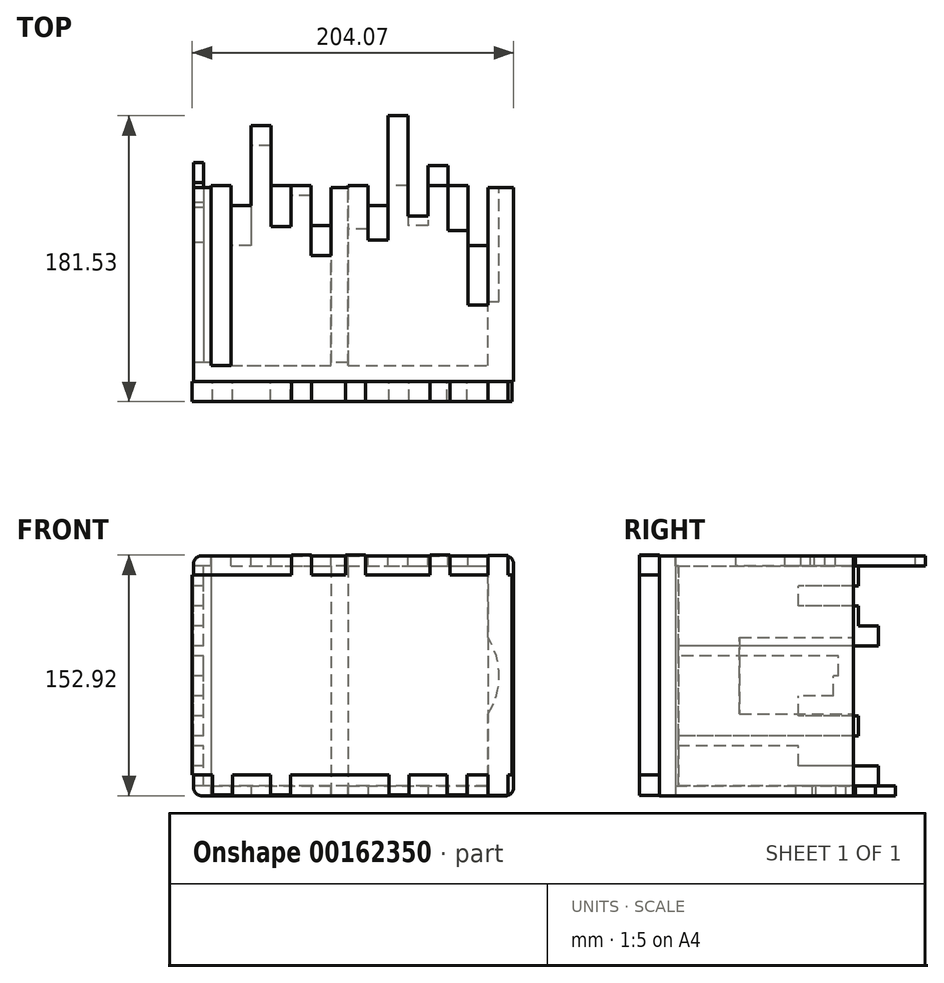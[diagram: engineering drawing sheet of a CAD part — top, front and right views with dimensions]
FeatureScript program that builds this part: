
annotation { "Feature Type Name" : "Feature", "Feature Type Description" : "" }
export const myFeature = defineFeature(function(context is Context, id is Id, definition is map)
    precondition{}
    {
        {
            var Q0;
            Q0=qCreatedBy(makeId("Front.planeOp"),FACE);
            var sketch = newSketch(context, id + "F0", { "sketchPlane" : qUnion([Q0])});
            skLineSegment(sketch, "E0.bottom", {"start": v(101.6, -76.2) * mm, "end": v(-101.6, -76.2) * mm});
            skLineSegment(sketch, "E0.top", {"start": v(101.6, 76.2) * mm, "end": v(-101.6, 76.2) * mm});
            skLineSegment(sketch, "E0.left", {"start": v(101.6, -76.2) * mm, "end": v(101.6, 76.2) * mm});
            skLineSegment(sketch, "E0.right", {"start": v(-101.6, -76.2) * mm, "end": v(-101.6, 76.2) * mm});
            skPoint(sketch, "E0.middle", {"position": v(0, 0) * mm});
            skSolve(sketch);
        }
        {
            var Q0;
            Q0=makeQuery(id+"F0.imprint","IMPRINT",FACE,{"disambiguationData":[TD([[makeQuery(id+"F0.imprint","IMPRINT",EDGE,{"derivedFrom":sQuery(id+"F0.wireOp",EDGE,"E0.bottom")}),-1.0]])]});
            var sketch = newSketch(context, id + "F1", { "sketchPlane" : qUnion([Q0])});
            skLineSegment(sketch, "E1.bottom", {"start": v(95.25, 69.94) * mm, "end": v(0, 69.94) * mm});
            skLineSegment(sketch, "E1.top", {"start": v(95.25, -69.76) * mm, "end": v(0, -69.76) * mm});
            skLineSegment(sketch, "E1.left", {"start": v(95.25, 69.94) * mm, "end": v(95.25, -69.76) * mm});
            skLineSegment(sketch, "E1.right", {"start": v(0, 69.94) * mm, "end": v(0, -69.76) * mm});
            skCircle(sketch, "E2", {"center": v(48.06, 0) * mm, "radius": 44.45 * mm});
            skSolve(sketch);
        }
        {
            var Q0;
            Q0=makeQuery(id+"F0.imprint","IMPRINT",FACE,{"disambiguationData":[TD([[makeQuery(id+"F0.imprint","IMPRINT",EDGE,{"derivedFrom":sQuery(id+"F0.wireOp",EDGE,"E0.bottom")}),-1.0]])]});
            extrude(context, id + "F2", {"entities" : qUnion([Q0]), "depth" : 152.4 * mm});
        }
        {
            var Q0;
            Q0=qCreatedBy(makeId("Front.planeOp"),FACE);
            var sketch = newSketch(context, id + "F3", { "sketchPlane" : qUnion([Q0])});
            skLineSegment(sketch, "E3.bottom", {"start": v(-6.15, 69.63) * mm, "end": v(-95.05, 69.63) * mm});
            skLineSegment(sketch, "E3.top", {"start": v(-6.15, -70.07) * mm, "end": v(-95.05, -70.07) * mm});
            skLineSegment(sketch, "E3.left", {"start": v(-6.15, 69.63) * mm, "end": v(-6.15, -70.07) * mm});
            skLineSegment(sketch, "E3.right", {"start": v(-95.05, 69.63) * mm, "end": v(-95.05, -70.07) * mm});
            skSolve(sketch);
        }
        {
            var Q0;
            Q0 = qSketchRegion(id + "F3", true);
            extrude(context, id + "F4", {"entities" : qUnion([Q0]), "operationType" : NewBodyOperationType.REMOVE, "depth" : 12.7 * mm});
        }
        {
            var Q0;
            Q0=makeQuery(id+"F4.boolean.opBoolean","COPY",FACE,{"derivedFrom":makeQuery(id+"F4.opExtrude","CAP_FACE",FACE,{"disambiguationData":[OSD([sQuery(id+"F3.wireOp",EDGE,"E3.bottom"),sQuery(id+"F3.wireOp",EDGE,"E3.top"),sQuery(id+"F3.wireOp",EDGE,"E3.left"),sQuery(id+"F3.wireOp",EDGE,"E3.right")])],"isStart":false})});
            var sketch = newSketch(context, id + "F5", { "sketchPlane" : qUnion([Q0])});
            skCircle(sketch, "E4", {"center": v(19.23, 52.88) * mm, "radius": 6.35 * mm});
            skCircle(sketch, "E5.0.1.0", {"center": v(19.23, 31.3) * mm, "radius": 6.35 * mm});
            skCircle(sketch, "E5.0.2.0", {"center": v(19.23, 9.7) * mm, "radius": 6.35 * mm});
            skCircle(sketch, "E5.0.3.0", {"center": v(19.23, -11.89) * mm, "radius": 6.35 * mm});
            skCircle(sketch, "E5.0.4.0", {"center": v(19.23, -33.48) * mm, "radius": 6.35 * mm});
            skCircle(sketch, "E5.0.5.0", {"center": v(19.23, -55.07) * mm, "radius": 6.35 * mm});
            skCircle(sketch, "E5.1.0.0", {"center": v(40.82, 52.88) * mm, "radius": 6.35 * mm});
            skCircle(sketch, "E5.1.1.0", {"center": v(40.82, 31.3) * mm, "radius": 6.35 * mm});
            skCircle(sketch, "E5.1.2.0", {"center": v(40.82, 9.7) * mm, "radius": 6.35 * mm});
            skCircle(sketch, "E5.1.3.0", {"center": v(40.82, -11.89) * mm, "radius": 6.35 * mm});
            skCircle(sketch, "E5.1.4.0", {"center": v(40.82, -33.48) * mm, "radius": 6.35 * mm});
            skCircle(sketch, "E5.1.5.0", {"center": v(40.82, -55.07) * mm, "radius": 6.35 * mm});
            skCircle(sketch, "E5.2.0.0", {"center": v(62.41, 52.88) * mm, "radius": 6.35 * mm});
            skCircle(sketch, "E5.2.1.0", {"center": v(62.41, 31.3) * mm, "radius": 6.35 * mm});
            skCircle(sketch, "E5.2.2.0", {"center": v(62.41, 9.7) * mm, "radius": 6.35 * mm});
            skCircle(sketch, "E5.2.3.0", {"center": v(62.41, -11.89) * mm, "radius": 6.35 * mm});
            skCircle(sketch, "E5.2.4.0", {"center": v(62.41, -33.48) * mm, "radius": 6.35 * mm});
            skCircle(sketch, "E5.2.5.0", {"center": v(62.41, -55.07) * mm, "radius": 6.35 * mm});
            skCircle(sketch, "E5.3.0.0", {"center": v(84, 52.88) * mm, "radius": 6.35 * mm});
            skCircle(sketch, "E5.3.1.0", {"center": v(84, 31.3) * mm, "radius": 6.35 * mm});
            skCircle(sketch, "E5.3.2.0", {"center": v(84, 9.7) * mm, "radius": 6.35 * mm});
            skCircle(sketch, "E5.3.3.0", {"center": v(84, -11.89) * mm, "radius": 6.35 * mm});
            skCircle(sketch, "E5.3.4.0", {"center": v(84, -33.48) * mm, "radius": 6.35 * mm});
            skCircle(sketch, "E5.3.5.0", {"center": v(84, -55.07) * mm, "radius": 6.35 * mm});
            skLineSegment(sketch, "E5.direction1", {"start": v(19.23, 52.88) * mm, "end": v(40.82, 52.88) * mm, "construction": true});
            skLineSegment(sketch, "E5.direction2", {"start": v(19.23, 52.88) * mm, "end": v(19.23, 31.3) * mm, "construction": true});
            skSolve(sketch);
        }
        {
            var Q0;
            Q0 = qSketchRegion(id + "F5", true);
            extrude(context, id + "F6", {"entities" : qUnion([Q0]), "operationType" : NewBodyOperationType.REMOVE, "oppositeDirection" : true, "depth" : 127 * mm});
        }
        {
            var Q0;
            Q0=makeQuery(id+"F2.opExtrude","CAP_FACE",FACE,{"disambiguationData":[OSD([sQuery(id+"F0.wireOp",EDGE,"E0.bottom"),sQuery(id+"F0.wireOp",EDGE,"E0.top"),sQuery(id+"F0.wireOp",EDGE,"E0.left"),sQuery(id+"F0.wireOp",EDGE,"E0.right")])],"isStart":false});
            var sketch = newSketch(context, id + "F7", { "sketchPlane" : qUnion([Q0])});
            skLineSegment(sketch, "E6.bottom", {"start": v(76.89, -54.4) * mm, "end": v(-76.89, -54.4) * mm});
            skLineSegment(sketch, "E6.top", {"start": v(76.89, 54.4) * mm, "end": v(-76.89, 54.4) * mm});
            skLineSegment(sketch, "E6.left", {"start": v(76.89, -54.4) * mm, "end": v(76.89, 54.4) * mm});
            skLineSegment(sketch, "E6.right", {"start": v(-76.89, -54.4) * mm, "end": v(-76.89, 54.4) * mm});
            skPoint(sketch, "E6.middle", {"position": v(0, 0) * mm});
            skSolve(sketch);
        }
        {
            var Q0;
            Q0=makeQuery(id+"F1.imprint","IMPRINT",FACE,{"disambiguationData":[TD([[makeQuery(id+"F1.imprint","IMPRINT",EDGE,{"derivedFrom":sQuery(id+"F1.wireOp",EDGE,"E2")}),1.0]])]});
            extrude(context, id + "F8", {"entities" : qUnion([Q0]), "operationType" : NewBodyOperationType.REMOVE, "depth" : 101.6 * mm});
        }
        {
            var Q0;
            Q0=makeQuery(id+"F2.opExtrude","CAP_EDGE",EDGE,{"disambiguationData":[OSD([sQuery(id+"F0.wireOp",EDGE,"E0.top")])],"isStart":true});
            var Q1;
            Q1=makeQuery(id+"F2.opExtrude","CAP_EDGE",EDGE,{"disambiguationData":[OSD([sQuery(id+"F0.wireOp",EDGE,"E0.left")])],"isStart":true});
            var Q2;
            Q2=makeQuery(id+"F2.opExtrude","CAP_EDGE",EDGE,{"disambiguationData":[OSD([sQuery(id+"F0.wireOp",EDGE,"E0.bottom")])],"isStart":true});
            var Q3;
            Q3=makeQuery(id+"F2.opExtrude","CAP_EDGE",EDGE,{"disambiguationData":[OSD([sQuery(id+"F0.wireOp",EDGE,"E0.right")])],"isStart":true});
            var Q4;
            Q4=makeQuery(id+"F2.opExtrude","SWEPT_EDGE",EDGE,{"disambiguationData":[OSD([sQuery(id+"F0.wireOp",EDGE,"E0.bottom"),sQuery(id+"F0.wireOp",EDGE,"E0.right")])]});
            var Q5;
            Q5=makeQuery(id+"F2.opExtrude","SWEPT_EDGE",EDGE,{"disambiguationData":[OSD([sQuery(id+"F0.wireOp",EDGE,"E0.bottom"),sQuery(id+"F0.wireOp",EDGE,"E0.left")])]});
            var Q6;
            Q6=makeQuery(id+"F2.opExtrude","SWEPT_EDGE",EDGE,{"disambiguationData":[OSD([sQuery(id+"F0.wireOp",EDGE,"E0.top"),sQuery(id+"F0.wireOp",EDGE,"E0.left")])]});
            var Q7;
            Q7=makeQuery(id+"F2.opExtrude","SWEPT_EDGE",EDGE,{"disambiguationData":[OSD([sQuery(id+"F0.wireOp",EDGE,"E0.top"),sQuery(id+"F0.wireOp",EDGE,"E0.right")])]});
            fillet(context, id + "F9", {"entities" : qUnion([Q0, Q1, Q2, Q3, Q4, Q5, Q6, Q7]), "radius" : 5.08 * mm, "tangentPropagation" : true, "allowEdgeOverflow" : false});
        }
        {
            var Q0;
            Q0=makeQuery(id+"F2.opExtrude","SWEPT_FACE",FACE,{"disambiguationData":[OSD([sQuery(id+"F0.wireOp",EDGE,"E0.right")])]});
            var sketch = newSketch(context, id + "F10", { "sketchPlane" : qUnion([Q0])});
            skLineSegment(sketch, "E7.bottom", {"start": v(140.43, -69.85) * mm, "end": v(13.43, -69.85) * mm});
            skLineSegment(sketch, "E7.top", {"start": v(140.43, 69.85) * mm, "end": v(13.43, 69.85) * mm});
            skLineSegment(sketch, "E7.left", {"start": v(140.43, -69.85) * mm, "end": v(140.43, 69.85) * mm});
            skLineSegment(sketch, "E7.right", {"start": v(13.43, -69.85) * mm, "end": v(13.43, 69.85) * mm});
            skPoint(sketch, "E7.middle", {"position": v(76.93, 0) * mm});
            skLineSegment(sketch, "E8.0.0", {"start": v(12.7, 69.63) * mm, "end": v(12.7, -70.07) * mm});
            skLineSegment(sketch, "E8.0.2", {"start": v(12.7, -70.07) * mm, "end": v(12.7, 69.63) * mm});
            skLineSegment(sketch, "E8.1.0", {"start": v(0, 71.12) * mm, "end": v(0, -71.12) * mm});
            skLineSegment(sketch, "E8.1.2", {"start": v(0, -71.12) * mm, "end": v(0, 71.12) * mm});
            skArc(sketch, "E8.2.0", {"start": v(0, 71.12) * mm, "mid": v(1.49, 74.71) * mm, "end": v(5.08, 76.2) * mm});
            skArc(sketch, "E8.2.2", {"start": v(5.08, 76.2) * mm, "mid": v(1.49, 74.71) * mm, "end": v(0, 71.12) * mm});
            skLineSegment(sketch, "E8.3.0", {"start": v(0, 71.12) * mm, "end": v(5.08, 71.12) * mm});
            skLineSegment(sketch, "E8.3.1", {"start": v(5.08, 71.12) * mm, "end": v(5.08, -71.12) * mm});
            skLineSegment(sketch, "E8.3.2", {"start": v(5.08, -71.12) * mm, "end": v(0, -71.12) * mm});
            skLineSegment(sketch, "E8.3.3", {"start": v(0, 71.12) * mm, "end": v(0, -71.12) * mm});
            skArc(sketch, "E8.4.0", {"start": v(5.08, -76.2) * mm, "mid": v(1.49, -74.71) * mm, "end": v(0, -71.12) * mm});
            skArc(sketch, "E8.4.2", {"start": v(0, -71.12) * mm, "mid": v(1.49, -74.71) * mm, "end": v(5.08, -76.2) * mm});
            skLineSegment(sketch, "E8.5.0", {"start": v(5.08, 71.12) * mm, "end": v(0, 71.12) * mm});
            skLineSegment(sketch, "E8.5.1", {"start": v(0, 71.12) * mm, "end": v(0, -71.12) * mm});
            skLineSegment(sketch, "E8.5.2", {"start": v(0, -71.12) * mm, "end": v(5.08, -71.12) * mm});
            skLineSegment(sketch, "E8.5.3", {"start": v(5.08, 71.12) * mm, "end": v(5.08, -71.12) * mm});
            skSolve(sketch);
        }
        {
            var Q0;
            Q0=makeQuery(id+"F10.imprint","IMPRINT",FACE,{"disambiguationData":[TD([[makeQuery(id+"F10.imprint","IMPRINT",EDGE,{"derivedFrom":sQuery(id+"F10.wireOp",EDGE,"E7.bottom")}),-1.0]])]});
            extrude(context, id + "F11", {"entities" : qUnion([Q0]), "operationType" : NewBodyOperationType.REMOVE, "oppositeDirection" : true, "depth" : 101.6 * mm});
        }
        {
            var Q0;
            Q0=makeQuery(id+"F2.opExtrude","CAP_FACE",FACE,{"disambiguationData":[OSD([sQuery(id+"F0.wireOp",EDGE,"E0.bottom"),sQuery(id+"F0.wireOp",EDGE,"E0.top"),sQuery(id+"F0.wireOp",EDGE,"E0.left"),sQuery(id+"F0.wireOp",EDGE,"E0.right")])],"isStart":true});
            var sketch = newSketch(context, id + "F12", { "sketchPlane" : qUnion([Q0])});
            skCircle(sketch, "E9", {"center": v(-87.4, 62.09) * mm, "radius": 6.35 * mm});
            skSolve(sketch);
        }
        {
            var Q0;
            Q0=makeQuery(id+"F2.opExtrude","SWEPT_FACE",FACE,{"disambiguationData":[OSD([sQuery(id+"F0.wireOp",EDGE,"E0.bottom")])]});
            var sketch = newSketch(context, id + "F13", { "sketchPlane" : qUnion([Q0])});
            skLineSegment(sketch, "E10.bottom", {"start": v(-90.54, 142.26) * mm, "end": v(-14.34, 142.26) * mm});
            skLineSegment(sketch, "E10.top", {"start": v(-90.54, 15.26) * mm, "end": v(-14.34, 15.26) * mm});
            skLineSegment(sketch, "E10.left", {"start": v(-90.54, 142.26) * mm, "end": v(-90.54, 15.26) * mm});
            skLineSegment(sketch, "E10.right", {"start": v(-14.34, 142.26) * mm, "end": v(-14.34, 15.26) * mm});
            skPoint(sketch, "E10.middle", {"position": v(-52.44, 78.76) * mm});
            skSolve(sketch);
        }
        {
            var Q0;
            Q0=makeQuery(id+"F12.imprint","IMPRINT",FACE,{"disambiguationData":[TD([[makeQuery(id+"F12.imprint","IMPRINT",EDGE,{"derivedFrom":sQuery(id+"F12.wireOp",EDGE,"E9")}),-1.0]])]});
            var sketch = newSketch(context, id + "F14", { "sketchPlane" : qUnion([Q0])});
            skLineSegment(sketch, "E11.bottom", {"start": v(-156.27, 104.96) * mm, "end": v(156.27, 104.96) * mm});
            skLineSegment(sketch, "E11.top", {"start": v(-156.27, -104.96) * mm, "end": v(156.27, -104.96) * mm});
            skLineSegment(sketch, "E11.left", {"start": v(-156.27, 104.96) * mm, "end": v(-156.27, -104.96) * mm});
            skLineSegment(sketch, "E11.right", {"start": v(156.27, 104.96) * mm, "end": v(156.27, -104.96) * mm});
            skPoint(sketch, "E11.middle", {"position": v(0, 0) * mm});
            skPoint(sketch, "E12.middle", {"position": v(298.59, 26.28) * mm});
            skSolve(sketch);
        }
        {
            var Q0;
            Q0=makeQuery(id+"F12.imprint","IMPRINT",FACE,{"disambiguationData":[TD([[makeQuery(id+"F12.imprint","IMPRINT",EDGE,{"derivedFrom":sQuery(id+"F12.wireOp",EDGE,"E9")}),-1.0]])]});
            var Q1;
            Q1=makeQuery(id+"F14.imprint","IMPRINT",FACE,{"disambiguationData":[TD([[makeQuery(id+"F14.imprint","IMPRINT",EDGE,{"derivedFrom":makeQuery(id+"F12.imprint","IMPRINT",EDGE,{"derivedFrom":makeQuery(id+"F4.boolean.opBoolean","COPY",EDGE,{"derivedFrom":makeQuery(id+"F4.opExtrude","CAP_EDGE",EDGE,{"disambiguationData":[OSD([sQuery(id+"F3.wireOp",EDGE,"E3.bottom")])],"isStart":true})})})}),-1.0]])]});
            var Q2;
            Q2 = qSketchRegion(id + "F14", true);
            extrude(context, id + "F15", {"entities" : qUnion([Q0, Q1, Q2]), "operationType" : NewBodyOperationType.REMOVE, "oppositeDirection" : true, "depth" : 29.2 * mm});
        }
        {
            var Q0;
            Q0 = qSketchRegion(id + "F13", true);
            extrude(context, id + "F16", {"entities" : qUnion([Q0]), "operationType" : NewBodyOperationType.REMOVE, "oppositeDirection" : true, "depth" : 152.4 * mm});
        }
        {
            var Q0;
            Q0=qCreatedBy(makeId("Top.planeOp"),FACE);
            var sketch = newSketch(context, id + "F17", { "sketchPlane" : qUnion([Q0])});
            skLineSegment(sketch, "E13.bottom", {"start": v(-3.6, -142.32) * mm, "end": v(85.3, -142.32) * mm});
            skLineSegment(sketch, "E13.top", {"start": v(-3.6, -15.32) * mm, "end": v(85.3, -15.32) * mm});
            skLineSegment(sketch, "E13.left", {"start": v(-3.6, -142.32) * mm, "end": v(-3.6, -15.32) * mm});
            skLineSegment(sketch, "E13.right", {"start": v(85.3, -142.32) * mm, "end": v(85.3, -15.32) * mm});
            skPoint(sketch, "E13.middle", {"position": v(40.84, -78.82) * mm});
            skSolve(sketch);
        }
        {
            var Q0;
            Q0 = qSketchRegion(id + "F17", true);
            extrude(context, id + "F18", {"entities" : qUnion([Q0]), "operationType" : NewBodyOperationType.REMOVE, "endBound" : BoundingType.SYMMETRIC, "depth" : 507.24 * mm});
        }
        {
            var Q0;
            Q0=makeQuery(id+"F2.opExtrude","SWEPT_FACE",FACE,{"disambiguationData":[OSD([sQuery(id+"F0.wireOp",EDGE,"E0.top")])]});
            var sketch = newSketch(context, id + "F19", { "sketchPlane" : qUnion([Q0])});
            skLineSegment(sketch, "E14.bottom", {"start": v(-90.54, -142.26) * mm, "end": v(-77.84, -142.26) * mm});
            skLineSegment(sketch, "E14.top", {"start": v(-90.54, -91.46) * mm, "end": v(-77.84, -91.46) * mm});
            skLineSegment(sketch, "E14.left", {"start": v(-90.54, -142.26) * mm, "end": v(-90.54, -91.46) * mm});
            skLineSegment(sketch, "E14.right", {"start": v(-77.84, -142.26) * mm, "end": v(-77.84, -91.46) * mm});
            skPoint(sketch, "E14.middle", {"position": v(-84.2, -116.86) * mm});
            skLineSegment(sketch, "E15.bottom", {"start": v(-77.84, -40.66) * mm, "end": v(-65.14, -40.66) * mm});
            skLineSegment(sketch, "E15.top", {"start": v(-77.84, -142.26) * mm, "end": v(-65.14, -142.26) * mm});
            skLineSegment(sketch, "E15.left", {"start": v(-77.84, -40.66) * mm, "end": v(-77.84, -142.26) * mm});
            skLineSegment(sketch, "E15.right", {"start": v(-65.14, -40.66) * mm, "end": v(-65.14, -142.26) * mm});
            skLineSegment(sketch, "E16.bottom", {"start": v(-65.14, 10.14) * mm, "end": v(-52.44, 10.14) * mm});
            skLineSegment(sketch, "E16.top", {"start": v(-65.14, -142.26) * mm, "end": v(-52.44, -142.26) * mm});
            skLineSegment(sketch, "E16.left", {"start": v(-65.14, 10.14) * mm, "end": v(-65.14, -142.26) * mm});
            skLineSegment(sketch, "E16.right", {"start": v(-52.44, 10.14) * mm, "end": v(-52.44, -142.26) * mm});
            skLineSegment(sketch, "E17.bottom", {"start": v(-52.44, -53.83) * mm, "end": v(-39.74, -53.83) * mm});
            skLineSegment(sketch, "E17.top", {"start": v(-52.44, -142.26) * mm, "end": v(-39.74, -142.26) * mm});
            skLineSegment(sketch, "E17.left", {"start": v(-52.44, -53.83) * mm, "end": v(-52.44, -142.26) * mm});
            skLineSegment(sketch, "E17.right", {"start": v(-39.74, -53.83) * mm, "end": v(-39.74, -142.26) * mm});
            skLineSegment(sketch, "E18.bottom", {"start": v(-39.74, -27.96) * mm, "end": v(-27.04, -27.96) * mm});
            skLineSegment(sketch, "E18.top", {"start": v(-39.74, -142.26) * mm, "end": v(-27.04, -142.26) * mm});
            skLineSegment(sketch, "E18.left", {"start": v(-39.74, -27.96) * mm, "end": v(-39.74, -142.26) * mm});
            skLineSegment(sketch, "E18.right", {"start": v(-27.04, -27.96) * mm, "end": v(-27.04, -142.26) * mm});
            skLineSegment(sketch, "E19.bottom", {"start": v(-27.04, -72.53) * mm, "end": v(-14.34, -72.53) * mm});
            skLineSegment(sketch, "E19.top", {"start": v(-27.04, -142.26) * mm, "end": v(-14.34, -142.26) * mm});
            skLineSegment(sketch, "E19.left", {"start": v(-27.04, -72.53) * mm, "end": v(-27.04, -142.26) * mm});
            skLineSegment(sketch, "E19.right", {"start": v(-14.34, -72.53) * mm, "end": v(-14.34, -142.26) * mm});
            skLineSegment(sketch, "E20.bottom", {"start": v(-3.6, -28.02) * mm, "end": v(9.1, -28.02) * mm});
            skLineSegment(sketch, "E20.top", {"start": v(-3.6, -142.32) * mm, "end": v(9.1, -142.32) * mm});
            skLineSegment(sketch, "E20.left", {"start": v(-3.6, -28.02) * mm, "end": v(-3.6, -142.32) * mm});
            skLineSegment(sketch, "E20.right", {"start": v(9.1, -28.02) * mm, "end": v(9.1, -142.32) * mm});
            skLineSegment(sketch, "E21.bottom", {"start": v(9.1, -62.44) * mm, "end": v(21.8, -62.44) * mm});
            skLineSegment(sketch, "E21.top", {"start": v(9.1, -142.32) * mm, "end": v(21.8, -142.32) * mm});
            skLineSegment(sketch, "E21.left", {"start": v(9.1, -62.44) * mm, "end": v(9.1, -142.32) * mm});
            skLineSegment(sketch, "E21.right", {"start": v(21.8, -62.44) * mm, "end": v(21.8, -142.32) * mm});
            skLineSegment(sketch, "E22.bottom", {"start": v(21.8, 16.43) * mm, "end": v(34.5, 16.43) * mm});
            skLineSegment(sketch, "E22.top", {"start": v(21.8, -142.32) * mm, "end": v(34.5, -142.32) * mm});
            skLineSegment(sketch, "E22.left", {"start": v(21.8, 16.43) * mm, "end": v(21.8, -142.32) * mm});
            skLineSegment(sketch, "E22.right", {"start": v(34.5, 16.43) * mm, "end": v(34.5, -142.32) * mm});
            skLineSegment(sketch, "E23.bottom", {"start": v(34.5, -47.24) * mm, "end": v(47.2, -47.24) * mm});
            skLineSegment(sketch, "E23.top", {"start": v(34.5, -142.32) * mm, "end": v(47.2, -142.32) * mm});
            skLineSegment(sketch, "E23.left", {"start": v(34.5, -47.24) * mm, "end": v(34.5, -142.32) * mm});
            skLineSegment(sketch, "E23.right", {"start": v(47.2, -47.24) * mm, "end": v(47.2, -142.32) * mm});
            skLineSegment(sketch, "E24.bottom", {"start": v(47.2, -28.02) * mm, "end": v(59.9, -28.02) * mm});
            skLineSegment(sketch, "E24.top", {"start": v(47.2, -142.32) * mm, "end": v(59.9, -142.32) * mm});
            skLineSegment(sketch, "E24.left", {"start": v(47.2, -28.02) * mm, "end": v(47.2, -142.32) * mm});
            skLineSegment(sketch, "E24.right", {"start": v(59.9, -28.02) * mm, "end": v(59.9, -142.32) * mm});
            skLineSegment(sketch, "E25.bottom", {"start": v(59.9, -56.63) * mm, "end": v(72.6, -56.63) * mm});
            skLineSegment(sketch, "E25.top", {"start": v(59.9, -142.32) * mm, "end": v(72.6, -142.32) * mm});
            skLineSegment(sketch, "E25.left", {"start": v(59.9, -56.63) * mm, "end": v(59.9, -142.32) * mm});
            skLineSegment(sketch, "E25.right", {"start": v(72.6, -56.63) * mm, "end": v(72.6, -142.32) * mm});
            skLineSegment(sketch, "E26.bottom", {"start": v(72.6, -103.72) * mm, "end": v(85.3, -103.72) * mm});
            skLineSegment(sketch, "E26.top", {"start": v(72.6, -142.32) * mm, "end": v(85.3, -142.32) * mm});
            skLineSegment(sketch, "E26.left", {"start": v(72.6, -103.72) * mm, "end": v(72.6, -142.32) * mm});
            skLineSegment(sketch, "E26.right", {"start": v(85.3, -103.72) * mm, "end": v(85.3, -142.32) * mm});
            skSolve(sketch);
        }
        {
            var Q0;
            Q0=makeQuery(id+"F19.imprint","IMPRINT",FACE,{"disambiguationData":[TD([[makeQuery(id+"F19.imprint","IMPRINT",EDGE,{"derivedFrom":sQuery(id+"F19.wireOp",EDGE,"E26.bottom")}),-1.0]])]});
            var Q1;
            {var subQ3=sQuery(id+"F19.wireOp",EDGE,"E24.bottom");Q1=makeQuery(id+"F19.imprint","IMPRINT",FACE,{"disambiguationData":[TD([[makeQuery(id+"F19.imprint","IMPRINT",EDGE,{"derivedFrom":subQ3}),-1.0]])]});}
            var Q2;
            Q2=makeQuery(id+"F19.imprint","IMPRINT",FACE,{"disambiguationData":[TD([[makeQuery(id+"F19.imprint","IMPRINT",EDGE,{"derivedFrom":sQuery(id+"F19.wireOp",EDGE,"E25.bottom")}),-1.0]])]});
            var Q3;
            {var subQ0=sQuery(id+"F19.wireOp",EDGE,"E23.bottom");Q3=makeQuery(id+"F19.imprint","IMPRINT",FACE,{"disambiguationData":[TD([[makeQuery(id+"F19.imprint","IMPRINT",EDGE,{"derivedFrom":subQ0}),-1.0]])]});}
            var Q4;
            {var subQ3=sQuery(id+"F19.wireOp",EDGE,"E22.bottom");Q4=makeQuery(id+"F19.imprint","IMPRINT",FACE,{"disambiguationData":[TD([[makeQuery(id+"F19.imprint","IMPRINT",EDGE,{"derivedFrom":subQ3}),-1.0]])]});}
            var Q5;
            {var subQ0=sQuery(id+"F19.wireOp",EDGE,"E21.bottom");Q5=makeQuery(id+"F19.imprint","IMPRINT",FACE,{"disambiguationData":[TD([[makeQuery(id+"F19.imprint","IMPRINT",EDGE,{"derivedFrom":subQ0}),-1.0]])]});}
            var Q6;
            Q6=makeQuery(id+"F19.imprint","IMPRINT",FACE,{"disambiguationData":[TD([[makeQuery(id+"F19.imprint","IMPRINT",EDGE,{"derivedFrom":sQuery(id+"F19.wireOp",EDGE,"E19.bottom")}),-1.0]])]});
            var Q7;
            {var subQ3=sQuery(id+"F19.wireOp",EDGE,"E18.bottom");Q7=makeQuery(id+"F19.imprint","IMPRINT",FACE,{"disambiguationData":[TD([[makeQuery(id+"F19.imprint","IMPRINT",EDGE,{"derivedFrom":subQ3}),-1.0]])]});}
            var Q8;
            {var subQ0=sQuery(id+"F19.wireOp",EDGE,"E17.bottom");Q8=makeQuery(id+"F19.imprint","IMPRINT",FACE,{"disambiguationData":[TD([[makeQuery(id+"F19.imprint","IMPRINT",EDGE,{"derivedFrom":subQ0}),-1.0]])]});}
            var Q9;
            {var subQ2=sQuery(id+"F19.wireOp",EDGE,"E16.bottom");Q9=makeQuery(id+"F19.imprint","IMPRINT",FACE,{"disambiguationData":[TD([[makeQuery(id+"F19.imprint","IMPRINT",EDGE,{"derivedFrom":subQ2}),-1.0]])]});}
            var Q10;
            {var subQ2=sQuery(id+"F19.wireOp",EDGE,"E15.bottom");Q10=makeQuery(id+"F19.imprint","IMPRINT",FACE,{"disambiguationData":[TD([[makeQuery(id+"F19.imprint","IMPRINT",EDGE,{"derivedFrom":subQ2}),-1.0]])]});}
            var Q11;
            {var subQ9=sQuery(id+"F19.wireOp",EDGE,"E20.bottom");Q11=makeQuery(id+"F19.imprint","IMPRINT",FACE,{"disambiguationData":[TD([[makeQuery(id+"F19.imprint","IMPRINT",EDGE,{"derivedFrom":subQ9}),-1.0]])]});}
            extrude(context, id + "F20", {"entities" : qUnion([Q0, Q1, Q2, Q3, Q4, Q5, Q6, Q7, Q8, Q9, Q10, Q11]), "operationType" : NewBodyOperationType.ADD, "oppositeDirection" : true, "depth" : 6.35 * mm});
        }
        {
            var Q0;
            Q0=makeQuery(id+"F2.opExtrude","SWEPT_FACE",FACE,{"disambiguationData":[OSD([sQuery(id+"F0.wireOp",EDGE,"E0.right")])]});
            var sketch = newSketch(context, id + "F21", { "sketchPlane" : qUnion([Q0])});
            skLineSegment(sketch, "E27.bottom", {"start": v(13.43, -69.85) * mm, "end": v(140.43, -69.85) * mm});
            skLineSegment(sketch, "E27.top", {"start": v(13.43, -57.15) * mm, "end": v(140.43, -57.15) * mm});
            skLineSegment(sketch, "E27.left", {"start": v(13.43, -69.85) * mm, "end": v(13.43, -57.15) * mm});
            skLineSegment(sketch, "E27.right", {"start": v(140.43, -69.85) * mm, "end": v(140.43, -57.15) * mm});
            skLineSegment(sketch, "E28.bottom", {"start": v(64.23, -57.15) * mm, "end": v(140.43, -57.15) * mm});
            skLineSegment(sketch, "E28.top", {"start": v(64.23, -44.45) * mm, "end": v(140.43, -44.45) * mm});
            skLineSegment(sketch, "E28.left", {"start": v(64.23, -57.15) * mm, "end": v(64.23, -44.45) * mm});
            skLineSegment(sketch, "E28.right", {"start": v(140.43, -57.15) * mm, "end": v(140.43, -44.45) * mm});
            skLineSegment(sketch, "E29.bottom", {"start": v(26.13, -38.1) * mm, "end": v(140.43, -38.1) * mm});
            skLineSegment(sketch, "E29.top", {"start": v(26.13, -25.4) * mm, "end": v(140.43, -25.4) * mm});
            skLineSegment(sketch, "E29.left", {"start": v(26.13, -38.1) * mm, "end": v(26.13, -25.4) * mm});
            skLineSegment(sketch, "E29.right", {"start": v(140.43, -38.1) * mm, "end": v(140.43, -25.4) * mm});
            skLineSegment(sketch, "E30.bottom", {"start": v(64.23, -25.4) * mm, "end": v(140.43, -25.4) * mm});
            skLineSegment(sketch, "E30.top", {"start": v(64.23, -12.7) * mm, "end": v(140.43, -12.7) * mm});
            skLineSegment(sketch, "E30.left", {"start": v(64.23, -25.4) * mm, "end": v(64.23, -12.7) * mm});
            skLineSegment(sketch, "E30.right", {"start": v(140.43, -25.4) * mm, "end": v(140.43, -12.7) * mm});
            skLineSegment(sketch, "E31.bottom", {"start": v(41.91, -12.7) * mm, "end": v(140.43, -12.7) * mm});
            skLineSegment(sketch, "E31.top", {"start": v(41.91, 0) * mm, "end": v(140.43, 0) * mm});
            skLineSegment(sketch, "E31.left", {"start": v(41.91, -12.7) * mm, "end": v(41.91, 0) * mm});
            skLineSegment(sketch, "E31.right", {"start": v(140.43, -12.7) * mm, "end": v(140.43, 0) * mm});
            skLineSegment(sketch, "E32.bottom", {"start": v(38.83, 0) * mm, "end": v(140.43, 0) * mm});
            skLineSegment(sketch, "E32.top", {"start": v(38.83, 12.7) * mm, "end": v(140.43, 12.7) * mm});
            skLineSegment(sketch, "E32.left", {"start": v(38.83, 0) * mm, "end": v(38.83, 12.7) * mm});
            skLineSegment(sketch, "E32.right", {"start": v(140.43, 0) * mm, "end": v(140.43, 12.7) * mm});
            skLineSegment(sketch, "E33.bottom", {"start": v(13.43, 19.05) * mm, "end": v(140.43, 19.05) * mm});
            skLineSegment(sketch, "E33.top", {"start": v(13.43, 31.75) * mm, "end": v(140.43, 31.75) * mm});
            skLineSegment(sketch, "E33.left", {"start": v(13.43, 19.05) * mm, "end": v(13.43, 31.75) * mm});
            skLineSegment(sketch, "E33.right", {"start": v(140.43, 19.05) * mm, "end": v(140.43, 31.75) * mm});
            skLineSegment(sketch, "E34.bottom", {"start": v(26.13, 31.75) * mm, "end": v(140.43, 31.75) * mm});
            skLineSegment(sketch, "E34.top", {"start": v(26.13, 44.45) * mm, "end": v(140.43, 44.45) * mm});
            skLineSegment(sketch, "E34.left", {"start": v(26.13, 31.75) * mm, "end": v(26.13, 44.45) * mm});
            skLineSegment(sketch, "E34.right", {"start": v(140.43, 31.75) * mm, "end": v(140.43, 44.45) * mm});
            skLineSegment(sketch, "E35.bottom", {"start": v(64.23, 44.45) * mm, "end": v(140.43, 44.45) * mm});
            skLineSegment(sketch, "E35.top", {"start": v(64.23, 57.15) * mm, "end": v(140.43, 57.15) * mm});
            skLineSegment(sketch, "E35.left", {"start": v(64.23, 44.45) * mm, "end": v(64.23, 57.15) * mm});
            skLineSegment(sketch, "E35.right", {"start": v(140.43, 44.45) * mm, "end": v(140.43, 57.15) * mm});
            skLineSegment(sketch, "E36.bottom", {"start": v(26.13, 57.15) * mm, "end": v(140.43, 57.15) * mm});
            skLineSegment(sketch, "E36.top", {"start": v(26.13, 69.85) * mm, "end": v(140.43, 69.85) * mm});
            skLineSegment(sketch, "E36.left", {"start": v(26.13, 57.15) * mm, "end": v(26.13, 69.85) * mm});
            skLineSegment(sketch, "E36.right", {"start": v(140.43, 57.15) * mm, "end": v(140.43, 69.85) * mm});
            skSolve(sketch);
        }
        {
            var Q0;
            Q0 = qSketchRegion(id + "F21", true);
            extrude(context, id + "F22", {"entities" : qUnion([Q0]), "operationType" : NewBodyOperationType.ADD, "oppositeDirection" : true, "depth" : 6.35 * mm});
        }
        {
            var Q0;
            Q0=makeQuery(id+"F2.opExtrude","SWEPT_FACE",FACE,{"disambiguationData":[OSD([sQuery(id+"F0.wireOp",EDGE,"E0.bottom")])]});
            var sketch = newSketch(context, id + "F23", { "sketchPlane" : qUnion([Q0])});
            skLineSegment(sketch, "E37.bottom", {"start": v(85.3, 66.12) * mm, "end": v(72.6, 66.12) * mm});
            skLineSegment(sketch, "E37.top", {"start": v(85.3, 142.32) * mm, "end": v(72.6, 142.32) * mm});
            skLineSegment(sketch, "E37.left", {"start": v(85.3, 66.12) * mm, "end": v(85.3, 142.32) * mm});
            skLineSegment(sketch, "E37.right", {"start": v(72.6, 66.12) * mm, "end": v(72.6, 142.32) * mm});
            skLineSegment(sketch, "E38.bottom", {"start": v(72.6, 28.02) * mm, "end": v(59.9, 28.02) * mm});
            skLineSegment(sketch, "E38.top", {"start": v(72.6, 142.32) * mm, "end": v(59.9, 142.32) * mm});
            skLineSegment(sketch, "E38.left", {"start": v(72.6, 28.02) * mm, "end": v(72.6, 142.32) * mm});
            skLineSegment(sketch, "E38.right", {"start": v(59.9, 28.02) * mm, "end": v(59.9, 142.32) * mm});
            skLineSegment(sketch, "E39.bottom", {"start": v(59.9, 15.32) * mm, "end": v(47.2, 15.32) * mm});
            skLineSegment(sketch, "E39.top", {"start": v(59.9, 142.32) * mm, "end": v(47.2, 142.32) * mm});
            skLineSegment(sketch, "E39.left", {"start": v(59.9, 15.32) * mm, "end": v(59.9, 142.32) * mm});
            skLineSegment(sketch, "E39.right", {"start": v(47.2, 15.32) * mm, "end": v(47.2, 142.32) * mm});
            skLineSegment(sketch, "E40.bottom", {"start": v(47.2, 53.42) * mm, "end": v(34.5, 53.42) * mm});
            skLineSegment(sketch, "E40.top", {"start": v(47.2, 142.32) * mm, "end": v(34.5, 142.32) * mm});
            skLineSegment(sketch, "E40.left", {"start": v(47.2, 53.42) * mm, "end": v(47.2, 142.32) * mm});
            skLineSegment(sketch, "E40.right", {"start": v(34.5, 53.42) * mm, "end": v(34.5, 142.32) * mm});
            skLineSegment(sketch, "E41.bottom", {"start": v(34.5, 28.02) * mm, "end": v(21.8, 28.02) * mm});
            skLineSegment(sketch, "E41.top", {"start": v(34.5, 142.32) * mm, "end": v(21.8, 142.32) * mm});
            skLineSegment(sketch, "E41.left", {"start": v(34.5, 28.02) * mm, "end": v(34.5, 142.32) * mm});
            skLineSegment(sketch, "E41.right", {"start": v(21.8, 28.02) * mm, "end": v(21.8, 142.32) * mm});
            skLineSegment(sketch, "E42.bottom", {"start": v(21.8, 40.72) * mm, "end": v(9.1, 40.72) * mm});
            skLineSegment(sketch, "E42.top", {"start": v(21.8, 142.32) * mm, "end": v(9.1, 142.32) * mm});
            skLineSegment(sketch, "E42.left", {"start": v(21.8, 40.72) * mm, "end": v(21.8, 142.32) * mm});
            skLineSegment(sketch, "E42.right", {"start": v(9.1, 40.72) * mm, "end": v(9.1, 142.32) * mm});
            skLineSegment(sketch, "E43.bottom", {"start": v(9.1, 55.59) * mm, "end": v(-3.6, 55.59) * mm});
            skLineSegment(sketch, "E43.top", {"start": v(9.1, 142.32) * mm, "end": v(-3.6, 142.32) * mm});
            skLineSegment(sketch, "E43.left", {"start": v(9.1, 55.59) * mm, "end": v(9.1, 142.32) * mm});
            skLineSegment(sketch, "E43.right", {"start": v(-3.6, 55.59) * mm, "end": v(-3.6, 142.32) * mm});
            skLineSegment(sketch, "E44.bottom", {"start": v(-14.34, 53.36) * mm, "end": v(-27.04, 53.36) * mm});
            skLineSegment(sketch, "E44.top", {"start": v(-14.34, 142.26) * mm, "end": v(-27.04, 142.26) * mm});
            skLineSegment(sketch, "E44.left", {"start": v(-14.34, 53.36) * mm, "end": v(-14.34, 142.26) * mm});
            skLineSegment(sketch, "E44.right", {"start": v(-27.04, 53.36) * mm, "end": v(-27.04, 142.26) * mm});
            skLineSegment(sketch, "E45.bottom", {"start": v(-27.04, 34.22) * mm, "end": v(-39.74, 34.22) * mm});
            skLineSegment(sketch, "E45.top", {"start": v(-27.04, 142.26) * mm, "end": v(-39.74, 142.26) * mm});
            skLineSegment(sketch, "E45.left", {"start": v(-27.04, 34.22) * mm, "end": v(-27.04, 142.26) * mm});
            skLineSegment(sketch, "E45.right", {"start": v(-39.74, 34.22) * mm, "end": v(-39.74, 142.26) * mm});
            skLineSegment(sketch, "E46.bottom", {"start": v(-39.74, 27.96) * mm, "end": v(-52.44, 27.96) * mm});
            skLineSegment(sketch, "E46.top", {"start": v(-39.74, 142.26) * mm, "end": v(-52.44, 142.26) * mm});
            skLineSegment(sketch, "E46.left", {"start": v(-39.74, 27.96) * mm, "end": v(-39.74, 142.26) * mm});
            skLineSegment(sketch, "E46.right", {"start": v(-52.44, 27.96) * mm, "end": v(-52.44, 142.26) * mm});
            skLineSegment(sketch, "E47.bottom", {"start": v(-52.44, 2.56) * mm, "end": v(-65.14, 2.56) * mm});
            skLineSegment(sketch, "E47.top", {"start": v(-52.44, 142.26) * mm, "end": v(-65.14, 142.26) * mm});
            skLineSegment(sketch, "E47.left", {"start": v(-52.44, 2.56) * mm, "end": v(-52.44, 142.26) * mm});
            skLineSegment(sketch, "E47.right", {"start": v(-65.14, 2.56) * mm, "end": v(-65.14, 142.26) * mm});
            skLineSegment(sketch, "E48.bottom", {"start": v(-65.14, 66.06) * mm, "end": v(-77.84, 66.06) * mm});
            skLineSegment(sketch, "E48.top", {"start": v(-65.14, 142.26) * mm, "end": v(-77.84, 142.26) * mm});
            skLineSegment(sketch, "E48.left", {"start": v(-65.14, 66.06) * mm, "end": v(-65.14, 142.26) * mm});
            skLineSegment(sketch, "E48.right", {"start": v(-77.84, 66.06) * mm, "end": v(-77.84, 142.26) * mm});
            skLineSegment(sketch, "E49.bottom", {"start": v(-77.84, 27.96) * mm, "end": v(-90.54, 27.96) * mm});
            skLineSegment(sketch, "E49.top", {"start": v(-77.84, 142.26) * mm, "end": v(-90.54, 142.26) * mm});
            skLineSegment(sketch, "E49.left", {"start": v(-77.84, 27.96) * mm, "end": v(-77.84, 142.26) * mm});
            skLineSegment(sketch, "E49.right", {"start": v(-90.54, 27.96) * mm, "end": v(-90.54, 142.26) * mm});
            skSolve(sketch);
        }
        {
            var Q0;
            {var subQ0=sQuery(id+"F23.wireOp",EDGE,"E37.bottom");Q0=makeQuery(id+"F23.imprint","IMPRINT",FACE,{"disambiguationData":[TD([[makeQuery(id+"F23.imprint","IMPRINT",EDGE,{"derivedFrom":subQ0}),-1.0]])]});}
            var Q1;
            Q1=makeQuery(id+"F23.imprint","IMPRINT",FACE,{"disambiguationData":[TD([[makeQuery(id+"F23.imprint","IMPRINT",EDGE,{"derivedFrom":sQuery(id+"F23.wireOp",EDGE,"E43.bottom")}),-1.0]])]});
            var Q2;
            {var subQ0=sQuery(id+"F23.wireOp",EDGE,"E44.bottom");Q2=makeQuery(id+"F23.imprint","IMPRINT",FACE,{"disambiguationData":[TD([[makeQuery(id+"F23.imprint","IMPRINT",EDGE,{"derivedFrom":subQ0}),-1.0]])]});}
            var Q3;
            {var subQ2=sQuery(id+"F23.wireOp",EDGE,"E38.bottom");Q3=makeQuery(id+"F23.imprint","IMPRINT",FACE,{"disambiguationData":[TD([[makeQuery(id+"F23.imprint","IMPRINT",EDGE,{"derivedFrom":subQ2}),-1.0]])]});}
            var Q4;
            {var subQ2=sQuery(id+"F23.wireOp",EDGE,"E39.bottom");Q4=makeQuery(id+"F23.imprint","IMPRINT",FACE,{"disambiguationData":[TD([[makeQuery(id+"F23.imprint","IMPRINT",EDGE,{"derivedFrom":subQ2}),-1.0]])]});}
            var Q5;
            {var subQ0=sQuery(id+"F23.wireOp",EDGE,"E40.bottom");Q5=makeQuery(id+"F23.imprint","IMPRINT",FACE,{"disambiguationData":[TD([[makeQuery(id+"F23.imprint","IMPRINT",EDGE,{"derivedFrom":subQ0}),-1.0]])]});}
            var Q6;
            {var subQ2=sQuery(id+"F23.wireOp",EDGE,"E41.bottom");Q6=makeQuery(id+"F23.imprint","IMPRINT",FACE,{"disambiguationData":[TD([[makeQuery(id+"F23.imprint","IMPRINT",EDGE,{"derivedFrom":subQ2}),-1.0]])]});}
            var Q7;
            Q7=makeQuery(id+"F23.imprint","IMPRINT",FACE,{"disambiguationData":[TD([[makeQuery(id+"F23.imprint","IMPRINT",EDGE,{"derivedFrom":sQuery(id+"F23.wireOp",EDGE,"E42.bottom")}),-1.0]])]});
            var Q8;
            {var subQ3=sQuery(id+"F23.wireOp",EDGE,"E45.bottom");Q8=makeQuery(id+"F23.imprint","IMPRINT",FACE,{"disambiguationData":[TD([[makeQuery(id+"F23.imprint","IMPRINT",EDGE,{"derivedFrom":subQ3}),-1.0]])]});}
            var Q9;
            {var subQ3=sQuery(id+"F23.wireOp",EDGE,"E46.bottom");Q9=makeQuery(id+"F23.imprint","IMPRINT",FACE,{"disambiguationData":[TD([[makeQuery(id+"F23.imprint","IMPRINT",EDGE,{"derivedFrom":subQ3}),-1.0]])]});}
            var Q10;
            {var subQ3=sQuery(id+"F23.wireOp",EDGE,"E47.bottom");Q10=makeQuery(id+"F23.imprint","IMPRINT",FACE,{"disambiguationData":[TD([[makeQuery(id+"F23.imprint","IMPRINT",EDGE,{"derivedFrom":subQ3}),-1.0]])]});}
            var Q11;
            {var subQ0=sQuery(id+"F23.wireOp",EDGE,"E48.bottom");Q11=makeQuery(id+"F23.imprint","IMPRINT",FACE,{"disambiguationData":[TD([[makeQuery(id+"F23.imprint","IMPRINT",EDGE,{"derivedFrom":subQ0}),-1.0]])]});}
            var Q12;
            {var subQ3=sQuery(id+"F23.wireOp",EDGE,"E49.bottom");Q12=makeQuery(id+"F23.imprint","IMPRINT",FACE,{"disambiguationData":[TD([[makeQuery(id+"F23.imprint","IMPRINT",EDGE,{"derivedFrom":subQ3}),-1.0]])]});}
            extrude(context, id + "F24", {"entities" : qUnion([Q0, Q1, Q2, Q3, Q4, Q5, Q6, Q7, Q8, Q9, Q10, Q11, Q12]), "oppositeDirection" : true, "depth" : 6.35 * mm});
        }
        {
            var Q0;
            Q0=makeQuery(id+"F7.imprint","IMPRINT",FACE,{"disambiguationData":[TD([[makeQuery(id+"F7.imprint","IMPRINT",EDGE,{"derivedFrom":sQuery(id+"F7.wireOp",EDGE,"E6.bottom")}),1.0]])]});
            var sketch = newSketch(context, id + "F25", { "sketchPlane" : qUnion([Q0])});
            skLineSegment(sketch, "E50.bottom", {"start": v(100.73, 64.02) * mm, "end": v(-102.47, 64.02) * mm});
            skLineSegment(sketch, "E50.top", {"start": v(100.73, -62.98) * mm, "end": v(-102.47, -62.98) * mm});
            skLineSegment(sketch, "E50.left", {"start": v(100.73, 64.02) * mm, "end": v(100.73, -62.98) * mm});
            skLineSegment(sketch, "E50.right", {"start": v(-102.47, 64.02) * mm, "end": v(-102.47, -62.98) * mm});
            skLineSegment(sketch, "E51.bottom", {"start": v(-26.67, 76.72) * mm, "end": v(-39.37, 76.72) * mm});
            skLineSegment(sketch, "E51.top", {"start": v(-26.67, 64.02) * mm, "end": v(-39.37, 64.02) * mm});
            skLineSegment(sketch, "E51.left", {"start": v(-26.67, 76.72) * mm, "end": v(-26.67, 64.02) * mm});
            skLineSegment(sketch, "E51.right", {"start": v(-39.37, 76.72) * mm, "end": v(-39.37, 64.02) * mm});
            skLineSegment(sketch, "E52.bottom", {"start": v(7.58, 76.72) * mm, "end": v(-5.12, 76.72) * mm});
            skLineSegment(sketch, "E52.top", {"start": v(7.58, 64.02) * mm, "end": v(-5.12, 64.02) * mm});
            skLineSegment(sketch, "E52.left", {"start": v(7.58, 76.72) * mm, "end": v(7.58, 64.02) * mm});
            skLineSegment(sketch, "E52.right", {"start": v(-5.12, 76.72) * mm, "end": v(-5.12, 64.02) * mm});
            skLineSegment(sketch, "E53.bottom", {"start": v(61.2, 76.72) * mm, "end": v(48.5, 76.72) * mm});
            skLineSegment(sketch, "E53.top", {"start": v(61.2, 64.02) * mm, "end": v(48.5, 64.02) * mm});
            skLineSegment(sketch, "E53.left", {"start": v(61.2, 76.72) * mm, "end": v(61.2, 64.02) * mm});
            skLineSegment(sketch, "E53.right", {"start": v(48.5, 76.72) * mm, "end": v(48.5, 64.02) * mm});
            skLineSegment(sketch, "E54.bottom", {"start": v(98.16, 76.44) * mm, "end": v(85.46, 76.44) * mm});
            skLineSegment(sketch, "E54.top", {"start": v(98.16, -75.96) * mm, "end": v(85.46, -75.96) * mm});
            skLineSegment(sketch, "E54.left", {"start": v(98.16, 76.44) * mm, "end": v(98.16, -75.96) * mm});
            skLineSegment(sketch, "E54.right", {"start": v(85.46, 76.44) * mm, "end": v(85.46, -75.96) * mm});
            skLineSegment(sketch, "E55.bottom", {"start": v(-89.77, -25.34) * mm, "end": v(-102.47, -25.34) * mm});
            skLineSegment(sketch, "E55.top", {"start": v(-89.77, -38.04) * mm, "end": v(-102.47, -38.04) * mm});
            skLineSegment(sketch, "E55.left", {"start": v(-89.77, -25.34) * mm, "end": v(-89.77, -38.04) * mm});
            skLineSegment(sketch, "E55.right", {"start": v(-102.47, -25.34) * mm, "end": v(-102.47, -38.04) * mm});
            skLineSegment(sketch, "E56.bottom", {"start": v(-89.77, 44.37) * mm, "end": v(-102.47, 44.37) * mm});
            skLineSegment(sketch, "E56.top", {"start": v(-89.77, 31.67) * mm, "end": v(-102.47, 31.67) * mm});
            skLineSegment(sketch, "E56.left", {"start": v(-89.77, 44.37) * mm, "end": v(-89.77, 31.67) * mm});
            skLineSegment(sketch, "E56.right", {"start": v(-102.47, 44.37) * mm, "end": v(-102.47, 31.67) * mm});
            skLineSegment(sketch, "E57.bottom", {"start": v(72.06, -62.98) * mm, "end": v(59.36, -62.98) * mm});
            skLineSegment(sketch, "E57.top", {"start": v(72.06, -75.68) * mm, "end": v(59.36, -75.68) * mm});
            skLineSegment(sketch, "E57.left", {"start": v(72.06, -62.98) * mm, "end": v(72.06, -75.68) * mm});
            skLineSegment(sketch, "E57.right", {"start": v(59.36, -62.98) * mm, "end": v(59.36, -75.68) * mm});
            skLineSegment(sketch, "E58.bottom", {"start": v(35.26, -62.98) * mm, "end": v(22.56, -62.98) * mm});
            skLineSegment(sketch, "E58.top", {"start": v(35.26, -75.68) * mm, "end": v(22.56, -75.68) * mm});
            skLineSegment(sketch, "E58.left", {"start": v(35.26, -62.98) * mm, "end": v(35.26, -75.68) * mm});
            skLineSegment(sketch, "E58.right", {"start": v(22.56, -62.98) * mm, "end": v(22.56, -75.68) * mm});
            skLineSegment(sketch, "E59.bottom", {"start": v(-40, -62.98) * mm, "end": v(-52.7, -62.98) * mm});
            skLineSegment(sketch, "E59.top", {"start": v(-40, -75.68) * mm, "end": v(-52.7, -75.68) * mm});
            skLineSegment(sketch, "E59.left", {"start": v(-40, -62.98) * mm, "end": v(-40, -75.68) * mm});
            skLineSegment(sketch, "E59.right", {"start": v(-52.7, -62.98) * mm, "end": v(-52.7, -75.68) * mm});
            skLineSegment(sketch, "E60.bottom", {"start": v(-76.74, -62.98) * mm, "end": v(-89.44, -62.98) * mm});
            skLineSegment(sketch, "E60.top", {"start": v(-76.74, -75.68) * mm, "end": v(-89.44, -75.68) * mm});
            skLineSegment(sketch, "E60.left", {"start": v(-76.74, -62.98) * mm, "end": v(-76.74, -75.68) * mm});
            skLineSegment(sketch, "E60.right", {"start": v(-89.44, -62.98) * mm, "end": v(-89.44, -75.68) * mm});
            skSolve(sketch);
        }
        {
            var Q0;
            Q0 = qSketchRegion(id + "F25", true);
            extrude(context, id + "F26", {"entities" : qUnion([Q0]), "operationType" : NewBodyOperationType.ADD, "depth" : 12.7 * mm});
        }
        {
            var Q0;
            {var subQ0=sQuery(id+"F1.wireOp",EDGE,"E2");var subQ2=sQuery(id+"F0.wireOp",EDGE,"E0.left");var subQ3=makeQuery(id+"F2.opExtrude","SWEPT_FACE",FACE,{"disambiguationData":[OSD([subQ2])]});var subQ4=sQuery(id+"F0.wireOp",EDGE,"E0.top");var subQ6=sQuery(id+"F0.wireOp",EDGE,"E0.bottom");Q0=makeQuery(id+"F18.boolean.opBoolean","SPLIT",FACE,{"disambiguationData":[TD([subQ3])],"derivedFrom":makeQuery(id+"F16.boolean.opBoolean","SPLIT",FACE,{"disambiguationData":[TD([subQ3])],"derivedFrom":makeQuery(id+"F15.boolean.opBoolean","TWEAK_FACE",FACE,{"derivedFrom":[makeQuery(id+"F15.opExtrude","CAP_FACE",FACE,{"disambiguationData":[OSD([subQ6,subQ4,subQ2,sQuery(id+"F0.wireOp",EDGE,"E0.right"),subQ0,sQuery(id+"F3.wireOp",EDGE,"E3.bottom"),sQuery(id+"F3.wireOp",EDGE,"E3.top"),sQuery(id+"F3.wireOp",EDGE,"E3.left"),sQuery(id+"F3.wireOp",EDGE,"E3.right"),sQuery(id+"F12.wireOp",EDGE,"E9")])],"isStart":false}),makeQuery(id+"F15.opExtrude","CAP_FACE",FACE,{"disambiguationData":[OSD([sQuery(id+"F14.wireOp",EDGE,"E11.bottom"),sQuery(id+"F14.wireOp",EDGE,"E11.top"),sQuery(id+"F14.wireOp",EDGE,"E11.left"),sQuery(id+"F14.wireOp",EDGE,"E11.right")])],"isStart":false})]})})});}
            var sketch = newSketch(context, id + "F27", { "sketchPlane" : qUnion([Q0])});
            skSolve(sketch);
        }
    });
